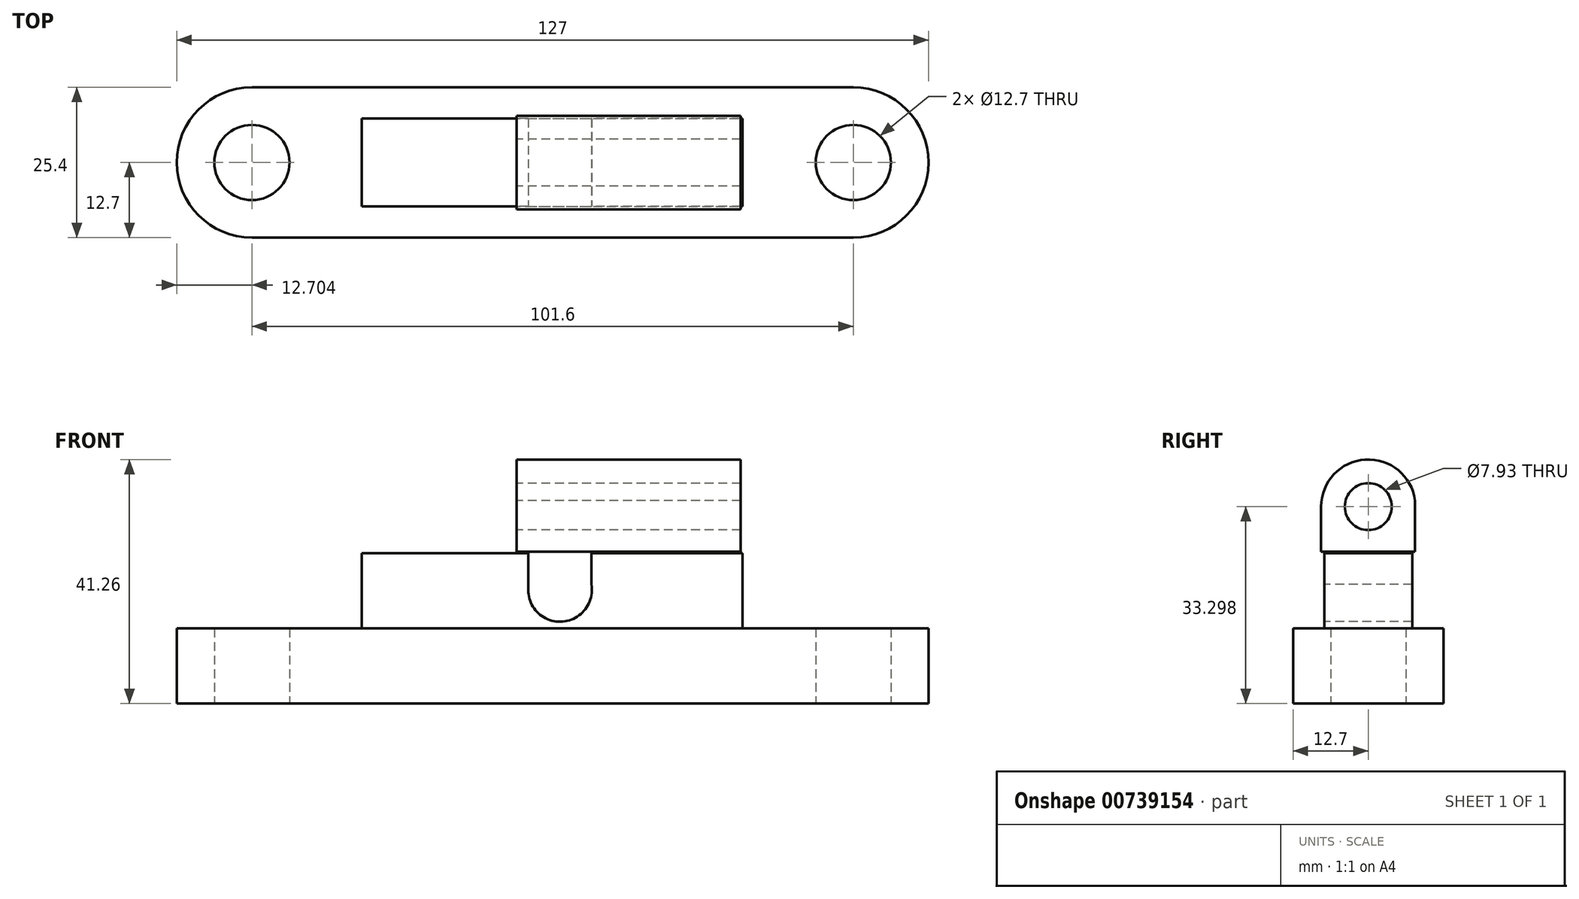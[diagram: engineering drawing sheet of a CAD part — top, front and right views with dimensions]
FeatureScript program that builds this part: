
annotation { "Feature Type Name" : "Feature", "Feature Type Description" : "" }
export const myFeature = defineFeature(function(context is Context, id is Id, definition is map)
    precondition{}
    {
        {
            var Q0;
            Q0=qCreatedBy(makeId("Top.planeOp"),FACE);
            var sketch = newSketch(context, id + "F0", { "sketchPlane" : qUnion([Q0])});
            skArc(sketch, "E0", {"start": v(-44.75, 12.7) * mm, "mid": v(-57.45, 0) * mm, "end": v(-44.75, -12.7) * mm});
            skArc(sketch, "E1", {"start": v(56.85, -12.7) * mm, "mid": v(69.55, 0) * mm, "end": v(56.85, 12.7) * mm});
            skLineSegment(sketch, "E2", {"start": v(-44.75, 12.7) * mm, "end": v(56.85, 12.7) * mm});
            skLineSegment(sketch, "E3", {"start": v(-44.75, -12.7) * mm, "end": v(56.85, -12.7) * mm});
            skCircle(sketch, "E4", {"center": v(-44.75, 0) * mm, "radius": 6.35 * mm});
            skCircle(sketch, "E5", {"center": v(56.85, 0) * mm, "radius": 6.35 * mm});
            skSolve(sketch);
        }
        {
            var Q0;
            Q0 = qSketchRegion(id + "F0", true);
            extrude(context, id + "F1", {"entities" : qUnion([Q0]), "depth" : 12.7 * mm, "offsetDistance" : 25.4 * mm});
        }
        {
            var Q0;
            Q0=qCreatedBy(makeId("Top.planeOp"),FACE);
            var sketch = newSketch(context, id + "F2", { "sketchPlane" : qUnion([Q0])});
            skLineSegment(sketch, "E6.bottom", {"start": v(38.15, 7.42) * mm, "end": v(-26.16, 7.42) * mm});
            skLineSegment(sketch, "E6.top", {"start": v(38.15, -7.42) * mm, "end": v(-26.16, -7.42) * mm});
            skLineSegment(sketch, "E6.left", {"start": v(38.15, 7.42) * mm, "end": v(38.15, -7.42) * mm});
            skLineSegment(sketch, "E6.right", {"start": v(-26.16, 7.42) * mm, "end": v(-26.16, -7.42) * mm});
            skPoint(sketch, "E6.middle", {"position": v(6, 0) * mm});
            skSolve(sketch);
        }
        {
            var Q0;
            Q0 = qSketchRegion(id + "F2", true);
            extrude(context, id + "F3", {"entities" : qUnion([Q0]), "operationType" : NewBodyOperationType.ADD, "depth" : 25.4 * mm, "offsetDistance" : 25.4 * mm});
        }
        {
            var Q0;
            Q0=makeQuery(id+"F3.opExtrude","SWEPT_FACE",FACE,{"disambiguationData":[OSD([sQuery(id+"F2.wireOp",EDGE,"E6.top")])]});
            var sketch = newSketch(context, id + "F4", { "sketchPlane" : qUnion([Q0])});
            skArc(sketch, "E7", {"start": v(1.92, 19.22) * mm, "mid": v(7.77, 13.87) * mm, "end": v(12.59, 20.17) * mm});
            skLineSegment(sketch, "E8", {"start": v(12.59, 20.17) * mm, "end": v(12.59, 25.4) * mm});
            skLineSegment(sketch, "E9", {"start": v(1.92, 19.22) * mm, "end": v(1.92, 25.4) * mm});
            skSolve(sketch);
        }
        {
            var Q0;
            Q0=makeQuery(id+"F4.imprint","IMPRINT",FACE,{"disambiguationData":[TD([[makeQuery(id+"F4.imprint","IMPRINT",EDGE,{"derivedFrom":sQuery(id+"F4.wireOp",EDGE,"E7")}),1.0]])]});
            extrude(context, id + "F5", {"entities" : qUnion([Q0]), "operationType" : NewBodyOperationType.REMOVE, "oppositeDirection" : true, "depth" : 25.4 * mm, "offsetDistance" : 25.4 * mm});
        }
        {
            var Q0;
            Q0=qCreatedBy(makeId("Right.planeOp"),FACE);
            var sketch = newSketch(context, id + "F6", { "sketchPlane" : qUnion([Q0])});
            skArc(sketch, "E10", {"start": v(-2.33, 25.69) * mm, "mid": v(0, 25.34) * mm, "end": v(2.33, 25.69) * mm});
            skLineSegment(sketch, "E11", {"start": v(-7.96, 33.3) * mm, "end": v(-7.96, 25.69) * mm});
            skLineSegment(sketch, "E12", {"start": v(-7.96, 25.69) * mm, "end": v(7.9, 25.69) * mm});
            skLineSegment(sketch, "E13", {"start": v(7.9, 25.69) * mm, "end": v(7.9, 34.3) * mm});
            skArc(sketch, "E14.trimOffspring", {"start": v(7.9, 32.3) * mm, "mid": v(0.5, 41.24) * mm, "end": v(-7.96, 33.3) * mm});
            skCircle(sketch, "E15", {"center": v(0, 33.3) * mm, "radius": 3.97 * mm});
            skSolve(sketch);
        }
        {
            var Q0;
            {var subQ6=sQuery(id+"F6.wireOp",EDGE,"E11");Q0=makeQuery(id+"F6.imprint","IMPRINT",FACE,{"disambiguationData":[TD([[makeQuery(id+"F6.imprint","IMPRINT",EDGE,{"derivedFrom":subQ6}),1.0]])]});}
            extrude(context, id + "F7", {"entities" : qUnion([Q0]), "depth" : 37.85 * mm, "offsetDistance" : 25.4 * mm});
        }
    });
